# Revit family: Doors_Sliding_Hajom_TypeG-Alu
name_source: partatom
category: Drzwi
revit_build: Autodesk Revit 2016 (Build: 20150220_1215(x64)
units: mm (PartAtom-declared; Revit-internal decimal feet)

## family parameters
Numer OmniClass = 23.30.10.00
Obiekt nadrzędny = Ściana
Punkt obliczania pomieszczeń = Nie
Tnij formami wycięć po wczytaniu = Nie
Tytuł OmniClass = Doors
Współdzielony = Nie
Zawsze pionowo = Tak

## types (1)
- Doors_Sliding_Hajom_TypeG-Alu
    BIMobject category = Sliding
    BIMobject category code = doors-sliding
    BIMobject main category = Doors
    BIMobject main category code = doors
    Brand url = https://hajom.com
    Design country = Sweden
    Door Image = Alu Green.png
    Edition number = 1
    Frame Projection Ext. = 25 mm  [stored 0.082021 ft]
    Frame Projection Int. = 25 mm  [stored 0.082021 ft]
    Frame Width = 75 mm  [stored 0.246063 ft]
    Funkcja = Wewnętrzna
    Grubość = 0 mm  [stored 0 ft]
    IFC Classification = Door
    Installation instructions = http://www.hajom.com
    Komentarze do typu = HAJOM ARCHITECT SERIES SLIDING DOORS
    Konstrukcja analityczna = <None>
    Manufacturer country = Sweden
    Manufacturer name = Hajom
    Masterformat 2014 Code = 08 32 19
    Masterformat 2014 Description = Sliding Wood-Framed Glass Doors
    Material main = Wood
    Material secondary = Glass
    Max Door Height = 2420 mm  [stored 7.93963 ft]
    Max Door Width = 6580 mm
    Min Door Height = 2020 mm  [stored 6.6273 ft]
    Min Door Width = 2980 mm  [stored 9.7769 ft]
    Model = Hajom Classic Typ A Alu
    OmniClass Code = 23-13 33 11
    OmniClass Description = Sliding Glass Wall Systems
    Producent = HAJOM
    Product Guid = ea730b45-3e54-4f74-ba85-31c2b9b06d4d
    Product SKU = TypG-Alu
    Product certification = http://www.hajom.com
    Product data url = https://bimobject.com
    Product family = Skjutdörrar
    Product group = Klassiska
    Product url = http://www.hajom.com
    QR code = http://bimobject.com
    Szerokość = 0 mm  [stored 0 ft]
    Szerokość brutto = 0 mm  [stored 0 ft]
    Technical description = http://www.hajom.com
    URL = http://www.hajom.com
    Uniclass 2015 Code = Ss_25_30_20_77
    Uniclass 2015 Name = Sliding doorset systems
    Uniformat II Code = B2030
    Uniformat II Description = Exterior Doors
    Wysokość = 0 mm  [stored 0 ft]
    Wysokość brutto = 0 mm  [stored 0 ft]
    Zakończenie ściany = Wg obiektu nadrzędnego

note: [stored X ft] marks values corroborated as IEEE doubles in the binary element streams (Revit-internal decimal feet)

## geometry (parser evidence)
native form markers: Blend x12, Sweep x17
no freeform markers — native parametric forms only
